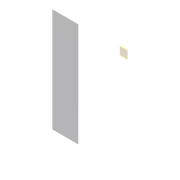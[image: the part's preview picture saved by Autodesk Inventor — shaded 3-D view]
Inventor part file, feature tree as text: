
AUTODESK INVENTOR PART (.ipt)
format: ipt  version: 2015 (Build 190159000, 159)  size: 23,337,472 bytes
history: native  units: in
note: dims shown in document units (in); Inventor stores cm internally (conversion verified against a paired STEP export)
features: other x2, sketch x2, plane x1, extrude x1
ambient origin geometry x8: Origin, YZ Plane, XZ Plane, XY Plane, X Axis, Y Axis, Z Axis, Center Point
bodies: Solid1 (feature_tree)
feature tree (6):
  plane  "Work Plane2"
  extrude  "Extrusion1"  [1 undecoded]
  other  "Decal1"
  sketch  "Sketch1"  dims[d0=0.0625in d1=0.0in]
  sketch  "Sketch2"
  other  "Image1"
note: 1 required parameter value undecoded (feature->parameter linkage not recoverable at this tier; creation-order binding heuristic only, values carry confidence <= 0.55)
